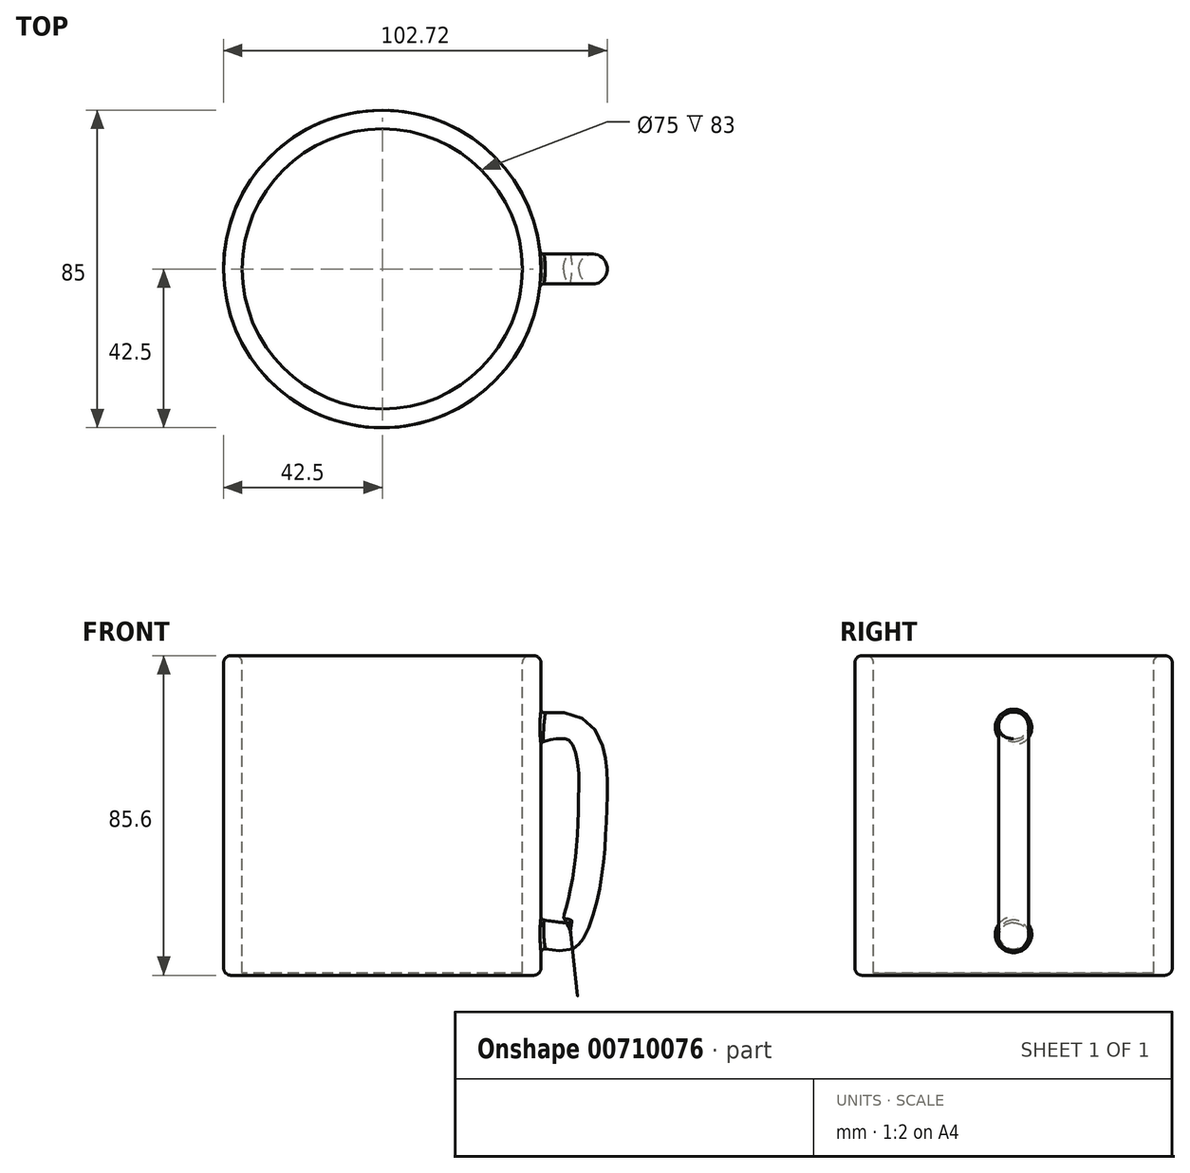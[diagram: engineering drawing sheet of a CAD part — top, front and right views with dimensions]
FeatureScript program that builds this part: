
annotation { "Feature Type Name" : "Feature", "Feature Type Description" : "" }
export const myFeature = defineFeature(function(context is Context, id is Id, definition is map)
    precondition{}
    {
        {
            var Q0;
            Q0=qCreatedBy(makeId("Top.planeOp"),FACE);
            var sketch = newSketch(context, id + "F0", { "sketchPlane" : qUnion([Q0])});
            skCircle(sketch, "E0", {"center": v(0, 0) * mm, "radius": 42.5 * mm});
            skSolve(sketch);
        }
        {
            var Q0;
            Q0=makeQuery(id+"F0.imprint","IMPRINT",FACE,{"disambiguationData":[TD([[makeQuery(id+"F0.imprint","IMPRINT",EDGE,{"derivedFrom":sQuery(id+"F0.wireOp",EDGE,"E0")}),1.0]])]});
            extrude(context, id + "F1", {"entities" : qUnion([Q0]), "depth" : 85.6 * mm, "offsetDistance" : 25 * mm});
        }
        {
            var Q0;
            Q0=makeQuery(id+"F1.opExtrude","CAP_FACE",FACE,{"disambiguationData":[OSD([sQuery(id+"F0.wireOp",EDGE,"E0")])],"isStart":false});
            var sketch = newSketch(context, id + "F2", { "sketchPlane" : qUnion([Q0])});
            skCircle(sketch, "E1", {"center": v(0, 0) * mm, "radius": 37.5 * mm});
            skSolve(sketch);
        }
        {
            var Q0;
            Q0 = qSketchRegion(id + "F2", true);
            extrude(context, id + "F3", {"entities" : qUnion([Q0]), "operationType" : NewBodyOperationType.REMOVE, "oppositeDirection" : true, "depth" : 85 * mm, "offsetDistance" : 25 * mm});
        }
        {
            var Q0;
            Q0=makeQuery(id+"F1.opExtrude","CAP_EDGE",EDGE,{"disambiguationData":[OSD([sQuery(id+"F0.wireOp",EDGE,"E0")])],"isStart":false});
            var Q1;
            Q1=makeQuery(id+"F1.opExtrude","CAP_FACE",FACE,{"disambiguationData":[OSD([sQuery(id+"F0.wireOp",EDGE,"E0")])],"isStart":false});
            var Q2;
            Q2=makeQuery(id+"F1.opExtrude","CAP_EDGE",EDGE,{"disambiguationData":[OSD([sQuery(id+"F0.wireOp",EDGE,"E0")])],"isStart":true});
            var Q3;
            Q3=makeQuery(id+"F3.boolean.opBoolean","COPY",EDGE,{"derivedFrom":makeQuery(id+"F3.opExtrude","CAP_EDGE",EDGE,{"disambiguationData":[OSD([sQuery(id+"F2.wireOp",EDGE,"E1")])],"isStart":true})});
            fillet(context, id + "F4", {"entities" : qUnion([Q0, Q1, Q2, Q3]), "radius" : 2 * mm, "tangentPropagation" : true, "allowEdgeOverflow" : false});
        }
        {
            var Q0;
            Q0=qCreatedBy(makeId("Front.planeOp"),FACE);
            var sketch = newSketch(context, id + "F5", { "sketchPlane" : qUnion([Q0])});
            skFitSpline(sketch, "E2", {"points": [v(39.55, 68.82) * mm, v(56.42, 65.98) * mm, v(59.81, 44.83) * mm, v(57.95, 23.65) * mm, v(52.36, 8.44) * mm, v(38.94, 8.03) * mm], "startDerivative": vector(101.68, 40.05) * mm, "endDerivative": vector(-143.78, 21.04) * mm});
            skSolve(sketch);
        }
        {
            var Q0;
            Q0=qCreatedBy(makeId("Right.planeOp"),FACE);
            cPlane(context, id + "F6", {"entities" : qUnion([Q0]), "cplaneType" : CPlaneType.OFFSET, "offset" : 40.8 * mm, "width" : 150 * mm, "height" : 150 * mm});
        }
        {
            var Q0;
            Q0=qCreatedBy(id+"F6.planeOp",FACE);
            var sketch = newSketch(context, id + "F7", { "sketchPlane" : qUnion([Q0])});
            skCircle(sketch, "E3", {"center": v(0, 65.57) * mm, "radius": 4 * mm});
            skSolve(sketch);
        }
        {
            var Q0;
            Q0 = qSketchRegion(id + "F7", true);
            var Q1;
            Q1 = qConstructionFilter(qBodyType(qCreatedBy(id + "F5" ,EDGE), BodyType.WIRE), ConstructionObject.NO);
            sweep(context, id + "F8", {"operationType" : NewBodyOperationType.ADD, "profiles" : qUnion([Q0]), "path" : qUnion([Q1])});
        }
        {
            var Q0;
            Q0=makeQuery(id+"F8.opSweep","SWEPT_FACE",FACE,{"disambiguationData":[OSD([sQuery(id+"F5.wireOp",EDGE,"E2"),sQuery(id+"F7.wireOp",EDGE,"E3")])]});
            fillet(context, id + "F9", {"entities" : qUnion([Q0]), "radius" : 1 * mm, "tangentPropagation" : true, "allowEdgeOverflow" : false});
        }
    });
